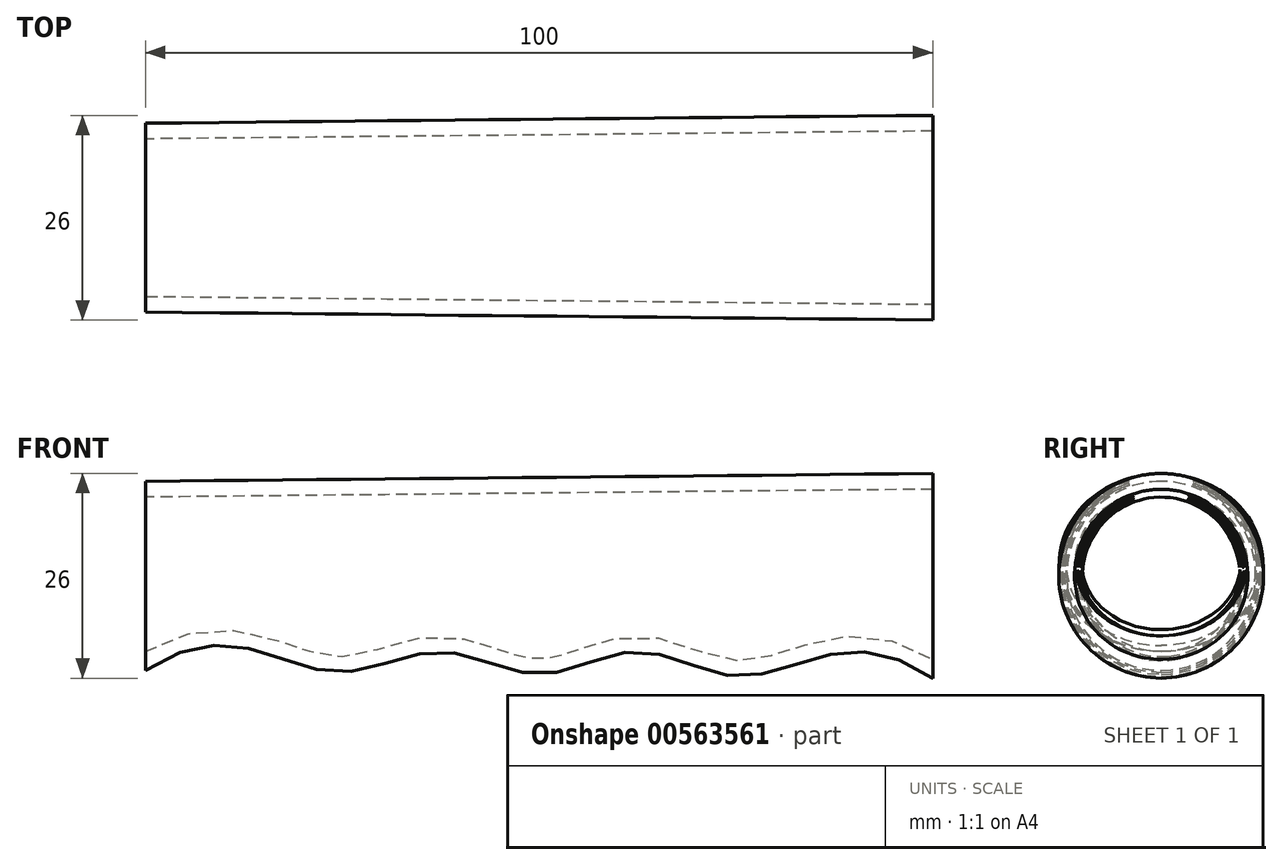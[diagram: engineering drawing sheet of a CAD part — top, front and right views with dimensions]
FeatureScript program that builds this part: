
annotation { "Feature Type Name" : "Feature", "Feature Type Description" : "" }
export const myFeature = defineFeature(function(context is Context, id is Id, definition is map)
    precondition{}
    {
        {
            var Q0;
            Q0=qCreatedBy(makeId("Right.planeOp"),FACE);
            var sketch = newSketch(context, id + "F0", { "sketchPlane" : qUnion([Q0])});
            skCircle(sketch, "E0", {"center": v(0, 0) * mm, "radius": 13 * mm});
            skLineSegment(sketch, "E1", {"start": v(0, -13) * mm, "end": v(0, 13) * mm, "construction": true});
            skSolve(sketch);
        }
        {
            var Q0;
            Q0=qCreatedBy(makeId("Right.planeOp"),FACE);
            cPlane(context, id + "F1", {"entities" : qUnion([Q0]), "cplaneType" : CPlaneType.OFFSET, "offset" : 100 * mm, "oppositeDirection" : true, "width" : 150 * mm, "height" : 150 * mm});
        }
        {
            var Q0;
            Q0=qCreatedBy(id+"F1.planeOp",FACE);
            var sketch = newSketch(context, id + "F2", { "sketchPlane" : qUnion([Q0])});
            skCircle(sketch, "E2", {"center": v(0, 0) * mm, "radius": 12 * mm});
            skLineSegment(sketch, "E3", {"start": v(0, -12) * mm, "end": v(0, 12) * mm, "construction": true});
            skSolve(sketch);
        }
        {
            var Q0;
            Q0=qCreatedBy(makeId("Front.planeOp"),FACE);
            var sketch = newSketch(context, id + "F3", { "sketchPlane" : qUnion([Q0])});
            skPoint(sketch, "E4.0", {"position": v(-100, 12) * mm});
            skPoint(sketch, "E5.0", {"position": v(-100, -12) * mm});
            skPoint(sketch, "E6.0", {"position": v(0, 13) * mm});
            skPoint(sketch, "E7.0", {"position": v(0, -13) * mm});
            skLineSegment(sketch, "E8", {"start": v(-100, 12) * mm, "end": v(0, 13) * mm});
            skLineSegment(sketch, "E9", {"start": v(-100, -12) * mm, "end": v(-75, -12.25) * mm, "construction": true});
            skLineSegment(sketch, "E10.0", {"start": v(-99.97, -9) * mm, "end": v(0.03, -10) * mm, "construction": true});
            skPoint(sketch, "E11", {"position": v(-50, -12.5) * mm});
            skLineSegment(sketch, "E12", {"start": v(-50, -12.5) * mm, "end": v(-25, -12.75) * mm, "construction": true});
            skPoint(sketch, "E13", {"position": v(-25, -12.75) * mm});
            skPoint(sketch, "E14", {"position": v(-75, -12.25) * mm});
            skLineSegment(sketch, "E15", {"start": v(-75, -12.25) * mm, "end": v(-50, -12.5) * mm, "construction": true});
            skLineSegment(sketch, "E16", {"start": v(-25, -12.75) * mm, "end": v(0, -13) * mm, "construction": true});
            skPoint(sketch, "E17", {"position": v(-12.5, -9.87) * mm});
            skPoint(sketch, "E17.positionSnap0", {"position": v(-12.5, -12.88) * mm});
            skPoint(sketch, "E18", {"position": v(-37.5, -9.62) * mm});
            skPoint(sketch, "E18.positionSnap0", {"position": v(-37.5, -12.62) * mm});
            skPoint(sketch, "E19", {"position": v(-62.5, -9.62) * mm});
            skPoint(sketch, "E19.positionSnap0", {"position": v(-62.5, -12.38) * mm});
            skPoint(sketch, "E20", {"position": v(-87.5, -9.12) * mm});
            skPoint(sketch, "E20.positionSnap0", {"position": v(-87.5, -12.12) * mm});
            skFitSpline(sketch, "E21", {"points": [v(0, -13) * mm, v(-12.5, -9.87) * mm, v(-25, -12.75) * mm, v(-37.5, -9.62) * mm, v(-50, -12.5) * mm, v(-62.5, -9.62) * mm, v(-75, -12.25) * mm, v(-87.5, -9.12) * mm, v(-100, -12) * mm], "startDerivative": vector(-99.62, 70.17) * mm, "endDerivative": vector(-100.24, -68.05) * mm});
            skSolve(sketch);
        }
        {
            var Q0;
            Q0=makeQuery(id+"F0.imprint","IMPRINT",FACE,{"disambiguationData":[TD([[makeQuery(id+"F0.imprint","IMPRINT",EDGE,{"derivedFrom":sQuery(id+"F0.wireOp",EDGE,"E0")}),1.0]])]});
            var Q1;
            Q1=makeQuery(id+"F2.imprint","IMPRINT",FACE,{"disambiguationData":[TD([[makeQuery(id+"F2.imprint","IMPRINT",EDGE,{"derivedFrom":sQuery(id+"F2.wireOp",EDGE,"E2")}),1.0]])]});
            var Q2;
            Q2=sQuery(id+"F3.wireOp",EDGE,"E21");
            var Q3;
            Q3=sQuery(id+"F3.wireOp",EDGE,"E8");
            loft(context, id + "F4", {"addGuides" : true, "sheetProfilesArray" : [{ "sheetProfileEntities" : qUnion([Q0]) }, { "sheetProfileEntities" : qUnion([Q1]) }], "guidesArray" : [{ "guideEntities" : qUnion([Q2]), "guideDerivativeType" : LoftGuideDerivativeType.DEFAULT, "guideDerivativeMagnitude" : 1 }, { "guideEntities" : qUnion([Q3]), "guideDerivativeType" : LoftGuideDerivativeType.DEFAULT, "guideDerivativeMagnitude" : 1 }]});
        }
        {
            var Q0;
            Q0=makeQuery(id+"F4.opLoft","CAP_FACE",FACE,{"disambiguationData":[OSD([makeQuery(id+"F2.imprint","IMPRINT",FACE,{"disambiguationData":[TD([[makeQuery(id+"F2.imprint","IMPRINT",EDGE,{"derivedFrom":sQuery(id+"F2.wireOp",EDGE,"E2")}),1.0]])]})])],"isStart":true});
            var Q1;
            Q1=makeQuery(id+"F4.opLoft","CAP_FACE",FACE,{"disambiguationData":[OSD([makeQuery(id+"F0.imprint","IMPRINT",FACE,{"disambiguationData":[TD([[makeQuery(id+"F0.imprint","IMPRINT",EDGE,{"derivedFrom":sQuery(id+"F0.wireOp",EDGE,"E0")}),1.0]])]})])],"isStart":true});
            shell(context, id + "F5", {"entities" : qUnion([Q0, Q1]), "thickness" : 2 * mm});
        }
    });
